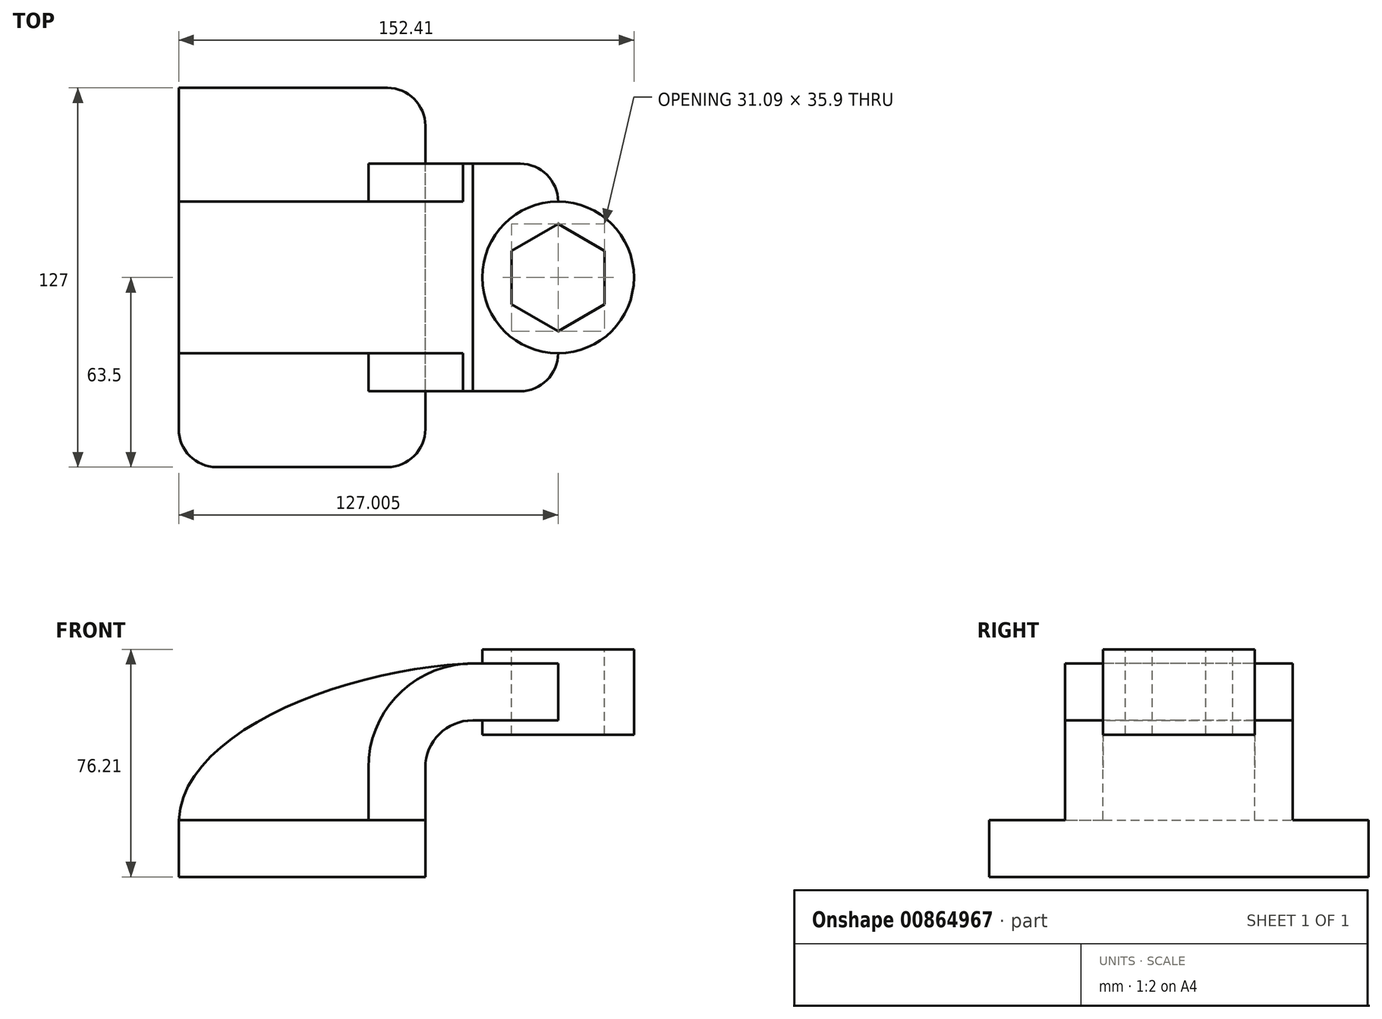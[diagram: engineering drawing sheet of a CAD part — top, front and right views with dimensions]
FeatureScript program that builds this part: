
annotation { "Feature Type Name" : "Feature", "Feature Type Description" : "" }
export const myFeature = defineFeature(function(context is Context, id is Id, definition is map)
    precondition{}
    {
        {
            var Q0;
            Q0=qCreatedBy(makeId("Front.planeOp"),FACE);
            var sketch = newSketch(context, id + "F0", { "sketchPlane" : qUnion([Q0])});
            skLineSegment(sketch, "E0.rect.bottom", {"start": v(-41.28, 9.52) * mm, "end": v(41.28, 9.52) * mm});
            skLineSegment(sketch, "E0.rect.top", {"start": v(-41.28, -9.52) * mm, "end": v(41.28, -9.52) * mm});
            skLineSegment(sketch, "E0.rect.left", {"start": v(-41.28, 9.52) * mm, "end": v(-41.28, -9.52) * mm});
            skLineSegment(sketch, "E0.rect.right", {"start": v(41.28, 9.52) * mm, "end": v(41.28, -9.52) * mm});
            skPoint(sketch, "E0.rect.middle", {"position": v(0, 0) * mm});
            skLineSegment(sketch, "E1", {"start": v(41.28, 9.52) * mm, "end": v(41.28, 27) * mm});
            skArc(sketch, "E2", {"start": v(41.28, 27) * mm, "mid": v(45.92, 38.23) * mm, "end": v(57.15, 42.88) * mm});
            skLineSegment(sketch, "E3", {"start": v(57.15, 42.88) * mm, "end": v(85.72, 42.88) * mm});
            skLineSegment(sketch, "E4.rect.bottom", {"start": v(60.32, 38.1) * mm, "end": v(111.12, 38.1) * mm});
            skLineSegment(sketch, "E4.rect.top", {"start": v(60.32, 66.68) * mm, "end": v(111.12, 66.68) * mm});
            skLineSegment(sketch, "E4.rect.left", {"start": v(60.32, 38.1) * mm, "end": v(60.32, 66.68) * mm});
            skLineSegment(sketch, "E4.rect.right", {"start": v(111.13, 38.1) * mm, "end": v(111.12, 66.68) * mm});
            skPoint(sketch, "E4.rect.middle", {"position": v(85.72, 52.39) * mm});
            skLineSegment(sketch, "E5.0", {"start": v(57.15, 61.93) * mm, "end": v(85.72, 61.93) * mm});
            skArc(sketch, "E5.1", {"start": v(22.23, 27) * mm, "mid": v(32.45, 51.7) * mm, "end": v(57.15, 61.93) * mm});
            skLineSegment(sketch, "E5.2", {"start": v(22.23, 9.52) * mm, "end": v(22.23, 27) * mm});
            skLineSegment(sketch, "E6", {"start": v(85.72, 38.1) * mm, "end": v(85.72, 66.68) * mm});
            skFitSpline(sketch, "E7", {"points": [v(-41.28, 9.53) * mm, v(57.15, 61.93) * mm], "startDerivative": vector(5.2, 92.34) * mm, "endDerivative": vector(120.92, 4.22) * mm});
            skSolve(sketch);
        }
        {
            var Q0;
            Q0=makeQuery(id+"F0.imprint","IMPRINT",FACE,{"disambiguationData":[TD([[makeQuery(id+"F0.imprint","IMPRINT",EDGE,{"derivedFrom":sQuery(id+"F0.wireOp",EDGE,"E0.rect.top")}),1.0]])]});
            extrude(context, id + "F1", {"entities" : qUnion([Q0]), "depth" : 127 * mm, "offsetDistance" : 25.4 * mm, "symmetric" : true});
        }
        {
            var Q0;
            {var subQ3=sQuery(id+"F0.wireOp",EDGE,"E5.2");Q0=makeQuery(id+"F0.imprint","IMPRINT",FACE,{"disambiguationData":[TD([[makeQuery(id+"F0.imprint","IMPRINT",EDGE,{"derivedFrom":subQ3}),1.0]])]});}
            extrude(context, id + "F2", {"entities" : qUnion([Q0]), "operationType" : NewBodyOperationType.ADD, "depth" : 50.8 * mm, "offsetDistance" : 25.4 * mm, "symmetric" : true});
        }
        {
            var Q0;
            {var subQ4=sQuery(id+"F0.wireOp",EDGE,"E1");Q0=makeQuery(id+"F0.imprint","IMPRINT",FACE,{"disambiguationData":[TD([[makeQuery(id+"F0.imprint","IMPRINT",EDGE,{"derivedFrom":subQ4}),1.0]])]});}
            var Q1;
            {var subQ0=sQuery(id+"F0.wireOp",EDGE,"E6");var subQ1=sQuery(id+"F0.wireOp",EDGE,"E3");var subQ2=makeQuery(id+"F0.imprint","INTERSECT",VERTEX,{"derivedFrom":[subQ1,subQ0]});Q1=makeQuery(id+"F0.imprint","IMPRINT",FACE,{"disambiguationData":[TD([[makeQuery(id+"F0.imprint","IMPRINT",EDGE,{"disambiguationData":[TD([[subQ2,1.0]])],"derivedFrom":subQ1}),1.0]])]});}
            extrude(context, id + "F3", {"entities" : qUnion([Q0, Q1]), "operationType" : NewBodyOperationType.ADD, "depth" : 76.2 * mm, "offsetDistance" : 25.4 * mm, "symmetric" : true});
        }
        {
            var Q0;
            {var subQ0=sQuery(id+"F0.wireOp",EDGE,"E4.rect.right");Q0=makeQuery(id+"F0.imprint","IMPRINT",FACE,{"disambiguationData":[TD([[makeQuery(id+"F0.imprint","IMPRINT",EDGE,{"derivedFrom":subQ0}),1.0]])]});}
            var Q1;
            Q1=sQuery(id+"F0.wireOp",EDGE,"E6");
            revolve(context, id + "F4", {"operationType" : NewBodyOperationType.ADD, "surfaceOperationType" : NewSurfaceOperationType.NEW, "entities" : qUnion([Q0]), "axis" : qUnion([Q1]), "revolveType" : RevolveType.FULL});
        }
        {
            var Q0;
            Q0=makeQuery(id+"F4.opRevolve","SWEPT_FACE",FACE,{"disambiguationData":[OSD([sQuery(id+"F0.wireOp",EDGE,"E4.rect.top")])]});
            var sketch = newSketch(context, id + "F5", { "sketchPlane" : qUnion([Q0])});
            skCircle(sketch, "E8.cCircle", {"center": v(85.72, 0) * mm, "radius": 15.55 * mm, "construction": true});
            skLineSegment(sketch, "E8.0", {"start": v(101.27, 8.98) * mm, "end": v(101.27, -8.98) * mm});
            skLineSegment(sketch, "E8.1", {"start": v(101.27, -8.98) * mm, "end": v(85.72, -17.95) * mm});
            skLineSegment(sketch, "E8.2", {"start": v(85.72, -17.95) * mm, "end": v(70.18, -8.98) * mm});
            skLineSegment(sketch, "E8.3", {"start": v(70.18, -8.98) * mm, "end": v(70.18, 8.98) * mm});
            skLineSegment(sketch, "E8.4", {"start": v(70.18, 8.98) * mm, "end": v(85.72, 17.95) * mm});
            skLineSegment(sketch, "E8.5", {"start": v(85.72, 17.95) * mm, "end": v(101.27, 8.98) * mm});
            skPoint(sketch, "E8.0.midPoint", {"position": v(101.27, 0) * mm});
            skSolve(sketch);
        }
        {
            var Q0;
            Q0 = qSketchRegion(id + "F5", true);
            extrude(context, id + "F6", {"entities" : qUnion([Q0]), "operationType" : NewBodyOperationType.REMOVE, "oppositeDirection" : true, "depth" : 91.19 * mm, "offsetDistance" : 25.4 * mm});
        }
        {
            var Q0;
            Q0=makeQuery(id+"F3.opExtrude","CAP_EDGE",EDGE,{"disambiguationData":[OSD([sQuery(id+"F0.wireOp",EDGE,"E6")])],"isStart":false});
            var Q1;
            Q1=makeQuery(id+"F3.opExtrude","CAP_EDGE",EDGE,{"disambiguationData":[OSD([sQuery(id+"F0.wireOp",EDGE,"E6")])],"isStart":true});
            var Q2;
            Q2=makeQuery(id+"F1.opExtrude","CAP_EDGE",EDGE,{"disambiguationData":[OSD([sQuery(id+"F0.wireOp",EDGE,"E0.rect.right")])],"isStart":false});
            var Q3;
            Q3=makeQuery(id+"F1.opExtrude","CAP_EDGE",EDGE,{"disambiguationData":[OSD([sQuery(id+"F0.wireOp",EDGE,"E0.rect.left")])],"isStart":false});
            var Q4;
            Q4=makeQuery(id+"F1.opExtrude","CAP_EDGE",EDGE,{"disambiguationData":[OSD([sQuery(id+"F0.wireOp",EDGE,"E0.rect.right")])],"isStart":true});
            fillet(context, id + "F7", {"entities" : qUnion([Q0, Q1, Q2, Q3, Q4]), "radius" : 12.7 * mm, "tangentPropagation" : true, "defaultsChanged" : true, "vertexSettings" : [], "allowEdgeOverflow" : false});
        }
    });
